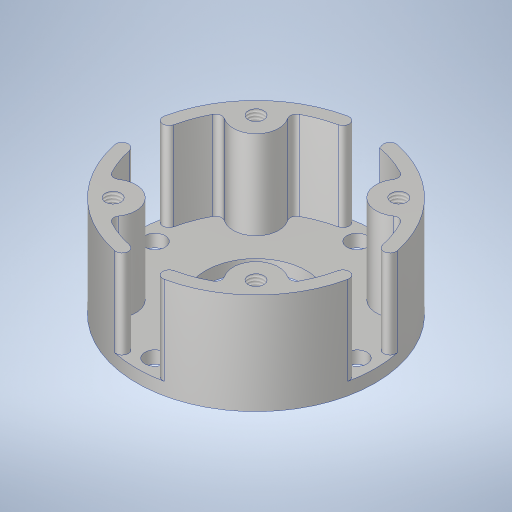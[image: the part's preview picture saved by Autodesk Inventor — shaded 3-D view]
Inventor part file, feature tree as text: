
AUTODESK INVENTOR PART (.ipt)
format: ipt  version: 2023.3 (Build 273359000, 359)  size: 384,512 bytes
history: native  units: in
note: dims shown in document units (in); Inventor stores cm internally (conversion verified against a paired STEP export)
features: sketch x5, extrude x4, projected_geometry x4, hole x2, fillet x1
ambient origin geometry x8: Origin, YZ Plane, XZ Plane, XY Plane, X Axis, Y Axis, Z Axis, Center Point
bodies: Solid1 (feature_tree)
feature tree (16):
  extrude  "Extrusion1"  Depth=2.36in
  hole  "Hole1"  [1 undecoded]
  extrude  "Extrusion2"  Depth=0.125in
  sketch  "Sketch4"  dims[d9=0.201in d10=0.75in d11=0.385in d12=0.25in d13=0.5635in d14=0.536in d15=0.8108in d16=0.125in]
  hole  "Hole2"  [1 undecoded]
  extrude  "Extrusion3"  Depth=1.0in
  fillet  "Fillet1"  Radius=0.375in
  extrude  "Extrusion4"  Depth=1.0in
  sketch  "Sketch1"  dims[d0=2.0in d1=2.36in]
  sketch  "Sketch2"  dims[d2=0.125in d3=0.0in d4=2.0in]
  sketch  "Sketch3"  dims[d5=3.1496in d7=360.0deg]
  projected_geometry  "Projected Loop1"
  projected_geometry  "Projected Loop2"
  projected_geometry  "Projected Loop3"
  projected_geometry  "Projected Loop4"
  sketch  "Sketch5"  dims[d25=0.875in d26=0.0in d27=0.156in d28=0.38in d29=0.375in d30=0.25in d31=0.5635in d32=1.0in d33=0.8108in d34=0.375in d35=0.375in d36=0.375in d37=0.375in d38=0.0in d39=0.0in d40=0.0625in d41=2.008in d42=1.0in d43=0.0in d44=0.0in]
note: 2 required parameter values undecoded (feature->parameter linkage not recoverable at this tier; creation-order binding heuristic only, values carry confidence <= 0.55)
